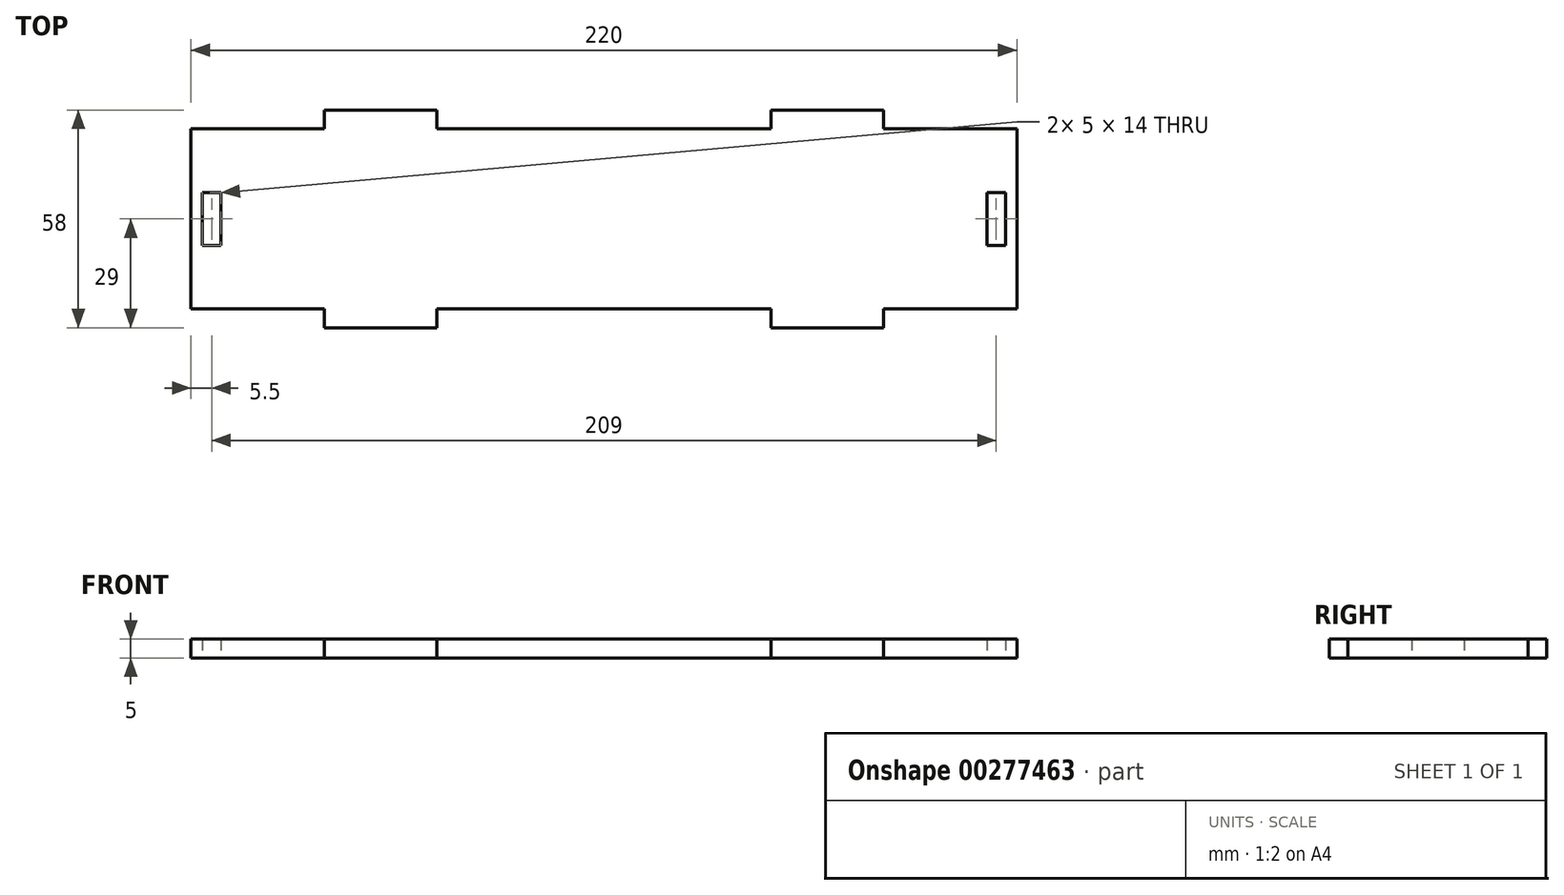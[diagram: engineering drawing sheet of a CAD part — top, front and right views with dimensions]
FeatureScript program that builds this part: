
annotation { "Feature Type Name" : "Feature", "Feature Type Description" : "" }
export const myFeature = defineFeature(function(context is Context, id is Id, definition is map)
    precondition{}
    {
        {
            var Q0;
            Q0=qCreatedBy(makeId("Top.planeOp"),FACE);
            var sketch = newSketch(context, id + "F0", { "sketchPlane" : qUnion([Q0])});
            skLineSegment(sketch, "E0.bottom", {"start": v(-110, 24) * mm, "end": v(-74.5, 24) * mm});
            skLineSegment(sketch, "E0.top", {"start": v(-110, -24) * mm, "end": v(-74.5, -24) * mm});
            skLineSegment(sketch, "E0.left", {"start": v(-110, 24) * mm, "end": v(-110, -24) * mm});
            skLineSegment(sketch, "E0.right", {"start": v(110, 24) * mm, "end": v(110, -24) * mm});
            skLineSegment(sketch, "E1.top", {"start": v(-74.5, 29) * mm, "end": v(-44.5, 29) * mm});
            skLineSegment(sketch, "E1.left", {"start": v(-74.5, 24) * mm, "end": v(-74.5, 29) * mm});
            skLineSegment(sketch, "E1.right", {"start": v(-44.5, 24) * mm, "end": v(-44.5, 29) * mm});
            skLineSegment(sketch, "E2.top", {"start": v(44.5, 29) * mm, "end": v(74.5, 29) * mm});
            skLineSegment(sketch, "E2.left", {"start": v(44.5, 24) * mm, "end": v(44.5, 29) * mm});
            skLineSegment(sketch, "E2.right", {"start": v(74.5, 24) * mm, "end": v(74.5, 29) * mm});
            skLineSegment(sketch, "E3.top", {"start": v(-74.5, -29) * mm, "end": v(-44.5, -29) * mm});
            skLineSegment(sketch, "E3.left", {"start": v(-74.5, -24) * mm, "end": v(-74.5, -29) * mm});
            skLineSegment(sketch, "E3.right", {"start": v(-44.5, -24) * mm, "end": v(-44.5, -29) * mm});
            skLineSegment(sketch, "E4.top", {"start": v(44.5, -29) * mm, "end": v(74.5, -29) * mm});
            skLineSegment(sketch, "E4.left", {"start": v(44.5, -24) * mm, "end": v(44.5, -29) * mm});
            skLineSegment(sketch, "E4.right", {"start": v(74.5, -24) * mm, "end": v(74.5, -29) * mm});
            skLineSegment(sketch, "E5.bottom", {"start": v(-107, 7) * mm, "end": v(-102, 7) * mm});
            skLineSegment(sketch, "E5.top", {"start": v(-107, -7) * mm, "end": v(-102, -7) * mm});
            skLineSegment(sketch, "E5.left", {"start": v(-107, 7) * mm, "end": v(-107, -7) * mm});
            skLineSegment(sketch, "E5.right", {"start": v(-102, 7) * mm, "end": v(-102, -7) * mm});
            skLineSegment(sketch, "E6.bottom", {"start": v(102, 7) * mm, "end": v(107, 7) * mm});
            skLineSegment(sketch, "E6.top", {"start": v(102, -7) * mm, "end": v(107, -7) * mm});
            skLineSegment(sketch, "E6.left", {"start": v(102, 7) * mm, "end": v(102, -7) * mm});
            skLineSegment(sketch, "E6.right", {"start": v(107, 7) * mm, "end": v(107, -7) * mm});
            skLineSegment(sketch, "E7.trimOffspring", {"start": v(-44.5, 24) * mm, "end": v(44.5, 24) * mm});
            skLineSegment(sketch, "E8.trimOffspring", {"start": v(74.5, 24) * mm, "end": v(110, 24) * mm});
            skLineSegment(sketch, "E9.trimOffspring", {"start": v(74.5, -24) * mm, "end": v(110, -24) * mm});
            skLineSegment(sketch, "E10.trimOffspring", {"start": v(-44.5, -24) * mm, "end": v(44.5, -24) * mm});
            skSolve(sketch);
        }
        {
            var Q0;
            Q0=makeQuery(id+"F0.imprint","IMPRINT",FACE,{"disambiguationData":[TD([[makeQuery(id+"F0.imprint","IMPRINT",EDGE,{"derivedFrom":sQuery(id+"F0.wireOp",EDGE,"E0.bottom")}),-1.0]])]});
            extrude(context, id + "F1", {"entities" : qUnion([Q0]), "depth" : 5 * mm});
        }
    });
